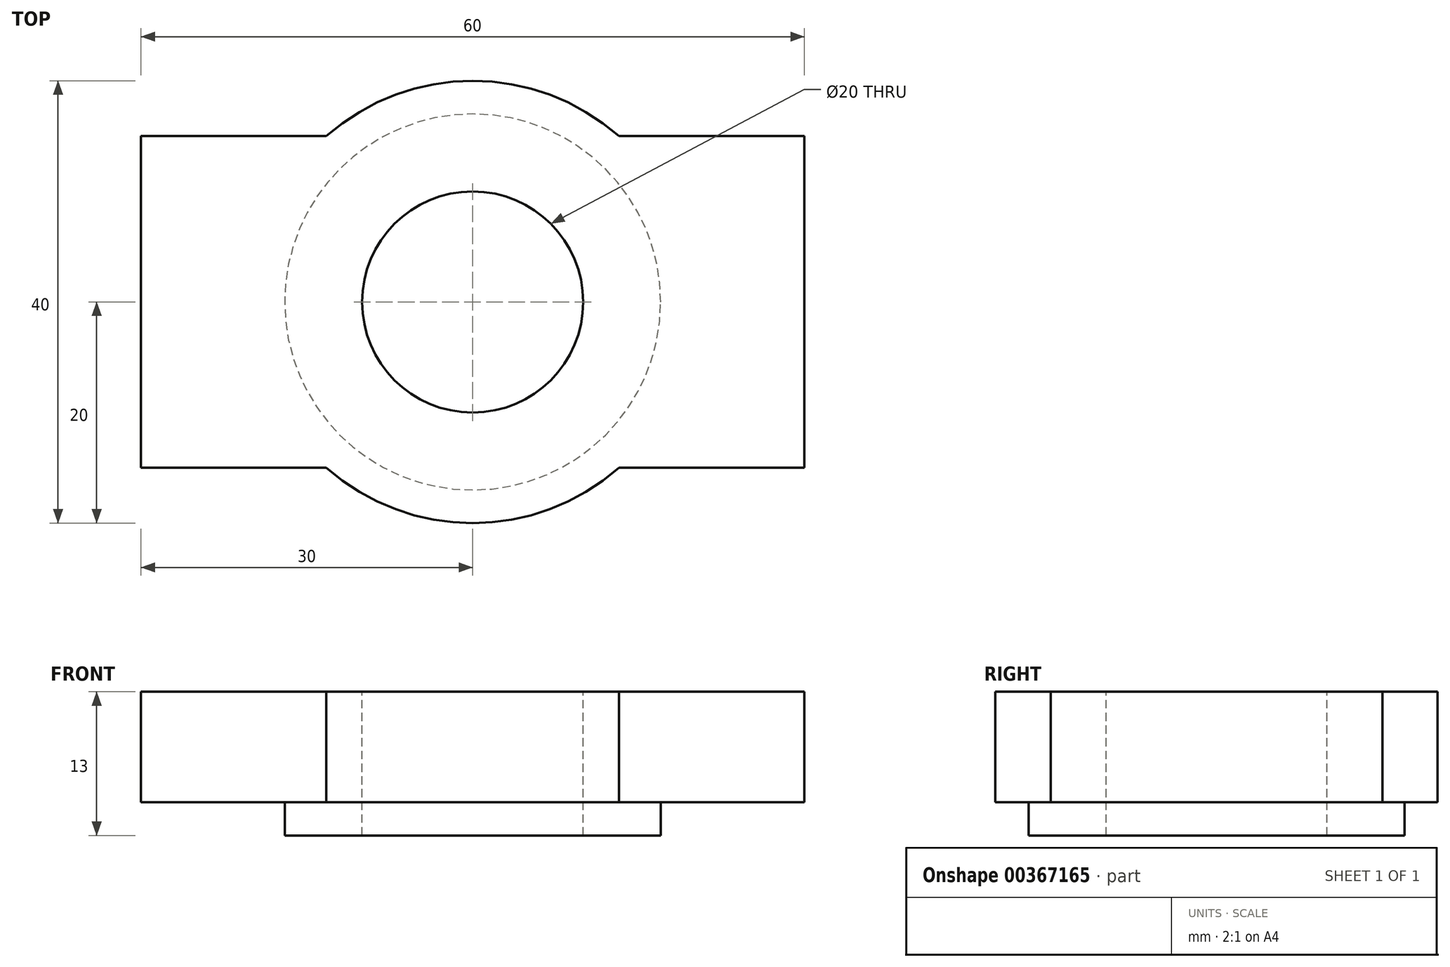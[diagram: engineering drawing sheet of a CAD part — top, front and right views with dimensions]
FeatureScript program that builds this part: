
annotation { "Feature Type Name" : "Feature", "Feature Type Description" : "" }
export const myFeature = defineFeature(function(context is Context, id is Id, definition is map)
    precondition{}
    {
        {
            var Q0;
            Q0=qCreatedBy(makeId("Front.planeOp"),FACE);
            var sketch = newSketch(context, id + "F0", { "sketchPlane" : qUnion([Q0])});
            skLineSegment(sketch, "E0", {"start": v(-20, 0) * mm, "end": v(20, 0) * mm});
            skLineSegment(sketch, "E1", {"start": v(20, 0) * mm, "end": v(20, 10) * mm});
            skLineSegment(sketch, "E2", {"start": v(20, 10) * mm, "end": v(-20, 10) * mm});
            skLineSegment(sketch, "E3", {"start": v(-20, 10) * mm, "end": v(-20, 0) * mm});
            skLineSegment(sketch, "E4", {"start": v(0, -14.13) * mm, "end": v(0, 19.6) * mm, "construction": true});
            skSolve(sketch);
        }
        {
            var Q0;
            Q0=makeQuery(id+"F0.imprint","IMPRINT",FACE,{"disambiguationData":[TD([[makeQuery(id+"F0.imprint","IMPRINT",EDGE,{"derivedFrom":sQuery(id+"F0.wireOp",EDGE,"E0")}),1.0]])]});
            extrude(context, id + "F1", {"entities" : qUnion([Q0]), "endBound" : BoundingType.SYMMETRIC, "depth" : 30 * mm});
        }
        {
            var Q0;
            Q0=makeQuery(id+"F1.opExtrude","SWEPT_FACE",FACE,{"disambiguationData":[OSD([sQuery(id+"F0.wireOp",EDGE,"E3")])]});
            var sketch = newSketch(context, id + "F2", { "sketchPlane" : qUnion([Q0])});
            skLineSegment(sketch, "E5", {"start": v(-15, 0) * mm, "end": v(15, 0) * mm});
            skLineSegment(sketch, "E6", {"start": v(15, 0) * mm, "end": v(15, 32) * mm});
            skLineSegment(sketch, "E7", {"start": v(-15, 0) * mm, "end": v(-15, 32) * mm});
            skArc(sketch, "E8", {"start": v(-15, 32) * mm, "mid": v(0, 47) * mm, "end": v(15, 32) * mm});
            skCircle(sketch, "E9", {"center": v(0, 32) * mm, "radius": 7.5 * mm});
            skSolve(sketch);
        }
        {
            var Q0;
            {var subQ0=sQuery(id+"F2.wireOp",EDGE,"E8");Q0=makeQuery(id+"F2.imprint","IMPRINT",FACE,{"disambiguationData":[TD([[makeQuery(id+"F2.imprint","IMPRINT",EDGE,{"derivedFrom":subQ0}),-1.0]])]});}
            var Q1;
            {var subQ0=sQuery(id+"F2.wireOp",EDGE,"E5");Q1=makeQuery(id+"F2.imprint","IMPRINT",FACE,{"disambiguationData":[TD([[makeQuery(id+"F2.imprint","IMPRINT",EDGE,{"derivedFrom":subQ0}),-1.0]])]});}
            extrude(context, id + "F3", {"entities" : qUnion([Q0, Q1]), "operationType" : NewBodyOperationType.ADD, "depth" : 10 * mm});
        }
        {
            var Q0;
            Q0=makeQuery(id+"F1.opExtrude","SWEPT_FACE",FACE,{"disambiguationData":[OSD([sQuery(id+"F0.wireOp",EDGE,"E1")])]});
            var sketch = newSketch(context, id + "F4", { "sketchPlane" : qUnion([Q0])});
            skLineSegment(sketch, "E10", {"start": v(-15, 0) * mm, "end": v(15, 0) * mm});
            skLineSegment(sketch, "E11", {"start": v(15, 0) * mm, "end": v(15, 32) * mm});
            skLineSegment(sketch, "E12", {"start": v(-15, 0) * mm, "end": v(-15, 32) * mm});
            skArc(sketch, "E13", {"start": v(-15, 32) * mm, "mid": v(0, 47) * mm, "end": v(15, 32) * mm});
            skCircle(sketch, "E14", {"center": v(0, 32) * mm, "radius": 7.5 * mm});
            skSolve(sketch);
        }
        {
            var Q0;
            {var subQ0=sQuery(id+"F4.wireOp",EDGE,"E13");Q0=makeQuery(id+"F4.imprint","IMPRINT",FACE,{"disambiguationData":[TD([[makeQuery(id+"F4.imprint","IMPRINT",EDGE,{"derivedFrom":subQ0}),-1.0]])]});}
            var Q1;
            {var subQ0=sQuery(id+"F4.wireOp",EDGE,"E10");Q1=makeQuery(id+"F4.imprint","IMPRINT",FACE,{"disambiguationData":[TD([[makeQuery(id+"F4.imprint","IMPRINT",EDGE,{"derivedFrom":subQ0}),1.0]])]});}
            extrude(context, id + "F5", {"entities" : qUnion([Q0, Q1]), "operationType" : NewBodyOperationType.ADD, "depth" : 10 * mm});
        }
        {
            var Q0;
            Q0=makeQuery(id+"F1.opExtrude","SWEPT_FACE",FACE,{"disambiguationData":[OSD([sQuery(id+"F0.wireOp",EDGE,"E2")])]});
            var sketch = newSketch(context, id + "F6", { "sketchPlane" : qUnion([Q0])});
            skLineSegment(sketch, "E15", {"start": v(0, -28.07) * mm, "end": v(0, 31.03) * mm, "construction": true});
            skPoint(sketch, "E15.endSnap0", {"position": v(0, 15) * mm});
            skArc(sketch, "E16", {"start": v(-13.23, -15) * mm, "mid": v(0, -20) * mm, "end": v(13.23, -15) * mm});
            skArc(sketch, "E17", {"start": v(13.23, 15) * mm, "mid": v(0, 20) * mm, "end": v(-13.23, 15) * mm});
            skSolve(sketch);
        }
        {
            var Q0;
            {var subQ0=sQuery(id+"F6.wireOp",EDGE,"E17");Q0=makeQuery(id+"F6.imprint","IMPRINT",FACE,{"disambiguationData":[TD([[makeQuery(id+"F6.imprint","IMPRINT",EDGE,{"derivedFrom":subQ0}),1.0]])]});}
            var Q1;
            {var subQ0=sQuery(id+"F6.wireOp",EDGE,"E16");Q1=makeQuery(id+"F6.imprint","IMPRINT",FACE,{"disambiguationData":[TD([[makeQuery(id+"F6.imprint","IMPRINT",EDGE,{"derivedFrom":subQ0}),1.0]])]});}
            extrude(context, id + "F7", {"entities" : qUnion([Q0, Q1]), "operationType" : NewBodyOperationType.ADD, "oppositeDirection" : true, "depth" : 10 * mm});
        }
        {
            var Q0;
            {var subQ0=sQuery(id+"F0.wireOp",EDGE,"E2");Q0=makeQuery(id+"F7.boolean.opBoolean","MERGE",FACE,{"derivedFrom":[makeQuery(id+"F1.opExtrude","SWEPT_FACE",FACE,{"disambiguationData":[OSD([subQ0])]}),makeQuery(id+"F7.opExtrude","CAP_FACE",FACE,{"disambiguationData":[OSD([subQ0,sQuery(id+"F6.wireOp",EDGE,"E16")])],"isStart":true}),makeQuery(id+"F7.opExtrude","CAP_FACE",FACE,{"disambiguationData":[OSD([subQ0,sQuery(id+"F6.wireOp",EDGE,"E17")])],"isStart":true})]});}
            var sketch = newSketch(context, id + "F8", { "sketchPlane" : qUnion([Q0])});
            skCircle(sketch, "E18", {"center": v(0, 0) * mm, "radius": 10 * mm});
            skSolve(sketch);
        }
        {
            var Q0;
            Q0=makeQuery(id+"F8.imprint","IMPRINT",FACE,{"disambiguationData":[TD([[makeQuery(id+"F8.imprint","IMPRINT",EDGE,{"derivedFrom":sQuery(id+"F8.wireOp",EDGE,"E18")}),1.0]])]});
            extrude(context, id + "F9", {"entities" : qUnion([Q0]), "operationType" : NewBodyOperationType.REMOVE, "endBound" : BoundingType.THROUGH_ALL, "oppositeDirection" : true, "depth" : 25 * mm});
        }
        {
            var Q0;
            {var subQ0=sQuery(id+"F0.wireOp",EDGE,"E2");Q0=makeQuery(id+"F7.boolean.opBoolean","MERGE",FACE,{"derivedFrom":[makeQuery(id+"F5.boolean.opBoolean","MERGE",FACE,{"derivedFrom":[makeQuery(id+"F3.boolean.opBoolean","MERGE",FACE,{"derivedFrom":[makeQuery(id+"F1.opExtrude","SWEPT_FACE",FACE,{"disambiguationData":[OSD([sQuery(id+"F0.wireOp",EDGE,"E0")])]}),makeQuery(id+"F3.opExtrude","SWEPT_FACE",FACE,{"disambiguationData":[OSD([sQuery(id+"F2.wireOp",EDGE,"E5")])]})]}),makeQuery(id+"F5.opExtrude","SWEPT_FACE",FACE,{"disambiguationData":[OSD([sQuery(id+"F4.wireOp",EDGE,"E10")])]})]}),makeQuery(id+"F7.opExtrude","CAP_FACE",FACE,{"disambiguationData":[OSD([subQ0,sQuery(id+"F6.wireOp",EDGE,"E16")])],"isStart":false}),makeQuery(id+"F7.opExtrude","CAP_FACE",FACE,{"disambiguationData":[OSD([subQ0,sQuery(id+"F6.wireOp",EDGE,"E17")])],"isStart":false})]});}
            var sketch = newSketch(context, id + "F10", { "sketchPlane" : qUnion([Q0])});
            skCircle(sketch, "E19", {"center": v(0, 0) * mm, "radius": 17 * mm});
            skSolve(sketch);
        }
        {
            var Q0;
            Q0=makeQuery(id+"F10.imprint","IMPRINT",FACE,{"disambiguationData":[TD([[makeQuery(id+"F10.imprint","IMPRINT",EDGE,{"derivedFrom":sQuery(id+"F10.wireOp",EDGE,"E19")}),1.0]])]});
            extrude(context, id + "F11", {"entities" : qUnion([Q0]), "operationType" : NewBodyOperationType.ADD, "depth" : 3 * mm});
        }
    });
